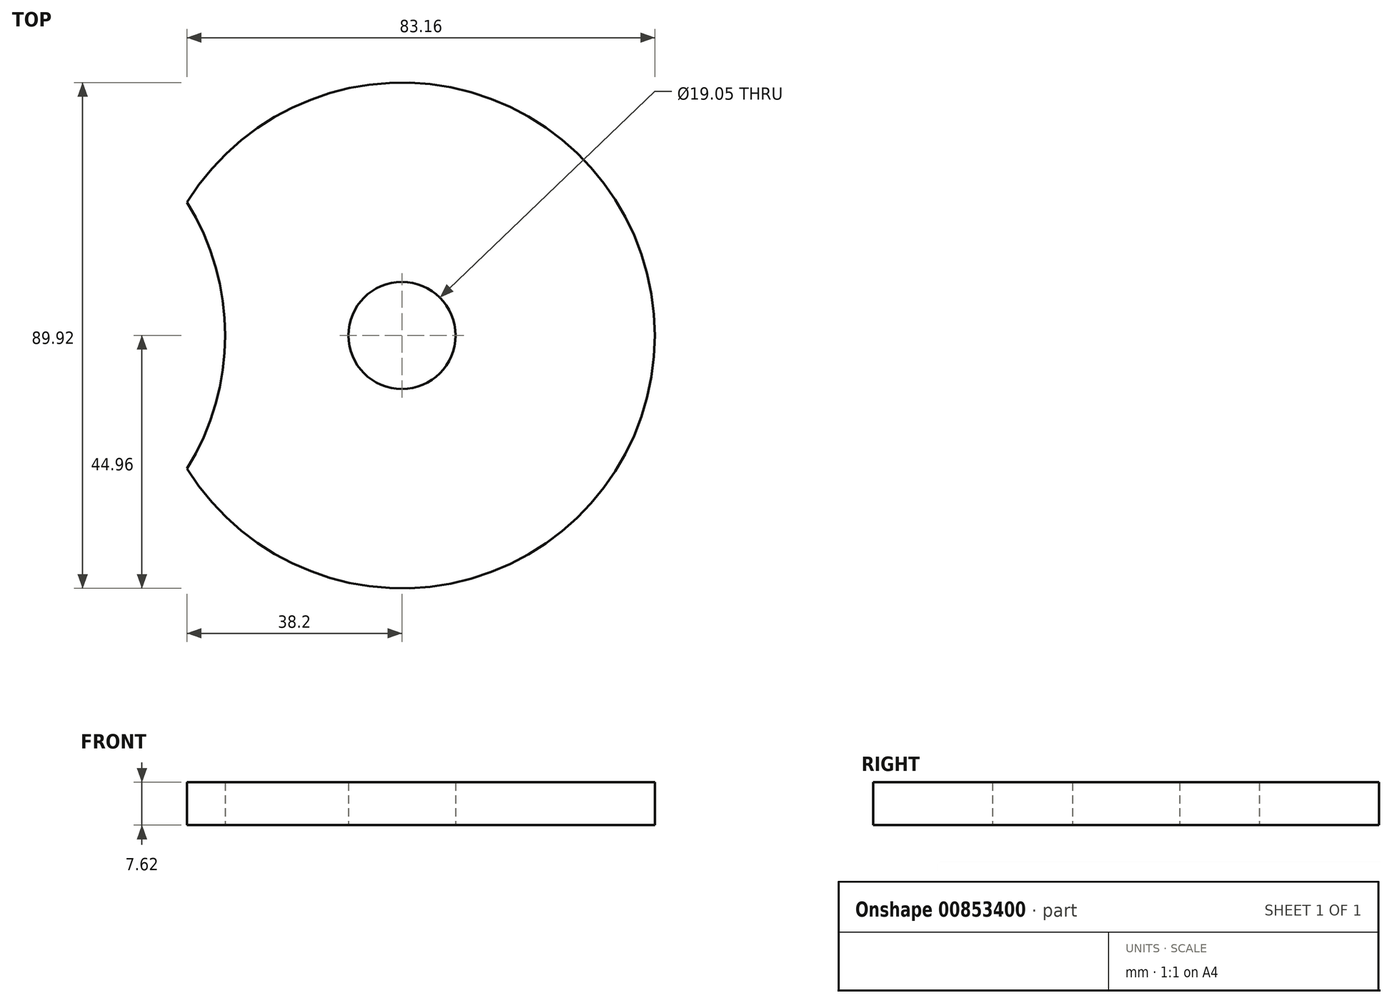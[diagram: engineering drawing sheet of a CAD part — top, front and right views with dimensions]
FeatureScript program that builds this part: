
annotation { "Feature Type Name" : "Feature", "Feature Type Description" : "" }
export const myFeature = defineFeature(function(context is Context, id is Id, definition is map)
    precondition{}
    {
        {
            var Q0;
            Q0=qCreatedBy(makeId("Top.planeOp"),FACE);
            var sketch = newSketch(context, id + "F0", { "sketchPlane" : qUnion([Q0])});
            skArc(sketch, "E0", {"start": v(-38.2, -23.71) * mm, "mid": v(44.96, 0) * mm, "end": v(-38.2, 23.71) * mm});
            skArc(sketch, "E1", {"start": v(-38.2, 23.71) * mm, "mid": v(-31.43, 0) * mm, "end": v(-38.2, -23.71) * mm});
            skSolve(sketch);
        }
        {
            var Q0;
            Q0 = qSketchRegion(id + "F0", true);
            extrude(context, id + "F1", {"entities" : qUnion([Q0]), "depth" : 7.62 * mm, "offsetDistance" : 25.4 * mm});
        }
        {
            var Q0;
            Q0=makeQuery(id+"F1.opExtrude","CAP_FACE",FACE,{"disambiguationData":[OSD([sQuery(id+"F0.wireOp",EDGE,"E0"),sQuery(id+"F0.wireOp",EDGE,"E1")])],"isStart":true});
            var sketch = newSketch(context, id + "F2", { "sketchPlane" : qUnion([Q0])});
            skCircle(sketch, "E2", {"center": v(0, 0) * mm, "radius": 9.53 * mm});
            skSolve(sketch);
        }
        {
            var Q0;
            Q0 = qSketchRegion(id + "F2", true);
            extrude(context, id + "F3", {"entities" : qUnion([Q0]), "operationType" : NewBodyOperationType.REMOVE, "oppositeDirection" : true, "depth" : 25.4 * mm, "offsetDistance" : 25.4 * mm});
        }
    });
